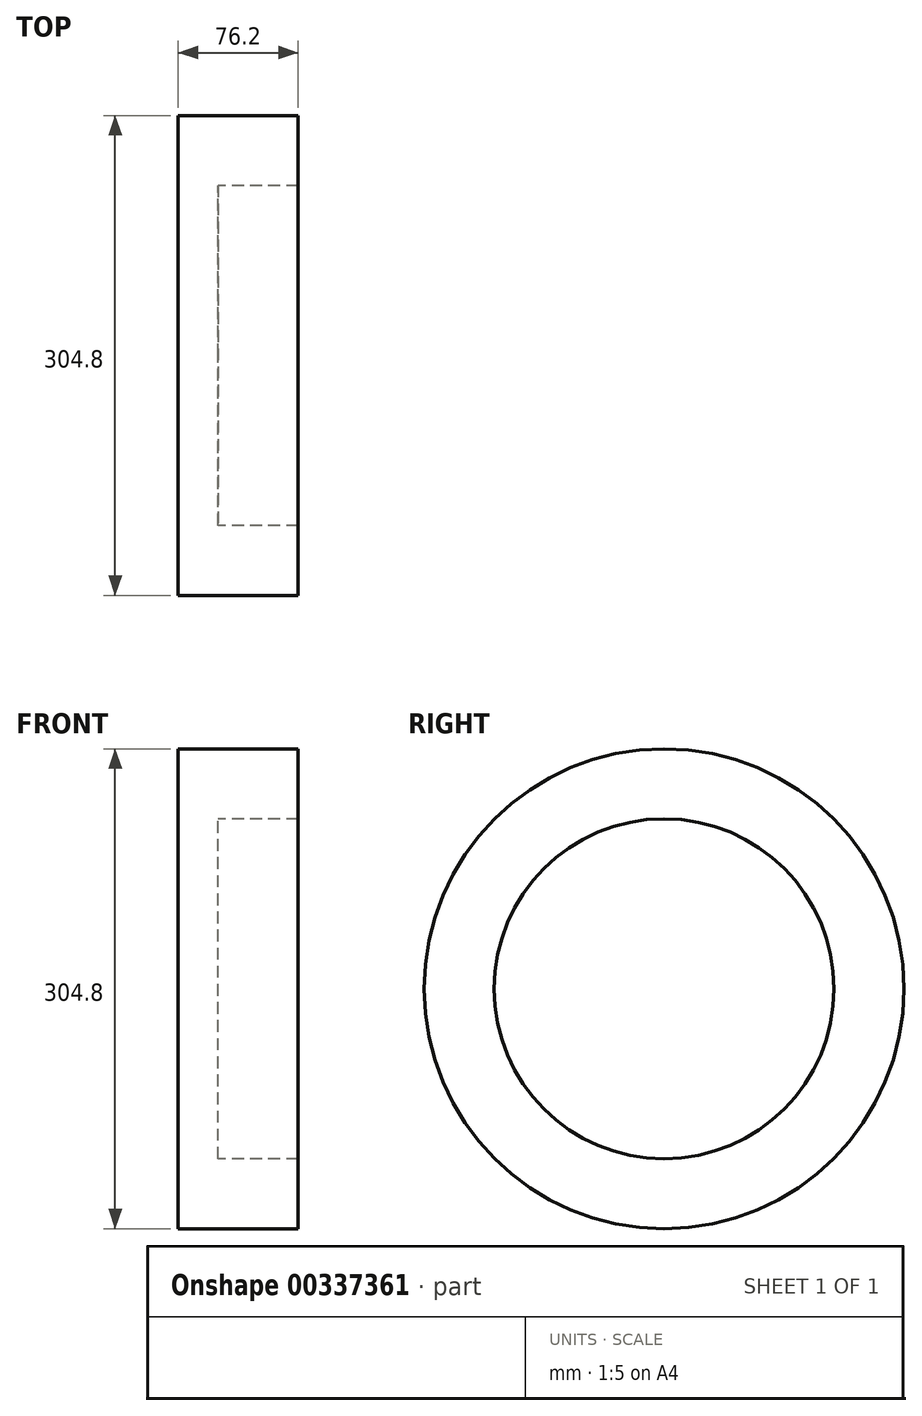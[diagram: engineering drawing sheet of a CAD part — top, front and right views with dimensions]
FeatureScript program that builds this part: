
annotation { "Feature Type Name" : "Feature", "Feature Type Description" : "" }
export const myFeature = defineFeature(function(context is Context, id is Id, definition is map)
    precondition{}
    {
        {
            var Q0;
            Q0=qCreatedBy(makeId("Right.planeOp"),FACE);
            var sketch = newSketch(context, id + "F0", { "sketchPlane" : qUnion([Q0])});
            skCircle(sketch, "E0", {"center": v(-57.45, 23.16) * mm, "radius": 152.4 * mm});
            skCircle(sketch, "E1", {"center": v(-57.45, 23.16) * mm, "radius": 107.95 * mm});
            skSolve(sketch);
        }
        {
            var Q0;
            Q0=makeQuery(id+"F0.imprint","IMPRINT",FACE,{"disambiguationData":[TD([[makeQuery(id+"F0.imprint","IMPRINT",EDGE,{"derivedFrom":sQuery(id+"F0.wireOp",EDGE,"E0")}),1.0]])]});
            extrude(context, id + "F1", {"entities" : qUnion([Q0]), "depth" : 76.2 * mm});
        }
        {
            var Q0;
            Q0=makeQuery(id+"F0.imprint","IMPRINT",FACE,{"disambiguationData":[TD([[makeQuery(id+"F0.imprint","IMPRINT",EDGE,{"derivedFrom":sQuery(id+"F0.wireOp",EDGE,"E1")}),1.0]])]});
            var sketch = newSketch(context, id + "F2", { "sketchPlane" : qUnion([Q0])});
            skSolve(sketch);
        }
        {
            var Q0;
            Q0 = qSketchRegion(id + "F2", true);
            var Q1;
            Q1=makeQuery(id+"F0.imprint","IMPRINT",FACE,{"disambiguationData":[TD([[makeQuery(id+"F0.imprint","IMPRINT",EDGE,{"derivedFrom":sQuery(id+"F0.wireOp",EDGE,"E1")}),1.0]])]});
            extrude(context, id + "F3", {"entities" : qUnion([Q0, Q1]), "operationType" : NewBodyOperationType.ADD, "depth" : 25.4 * mm});
        }
    });
